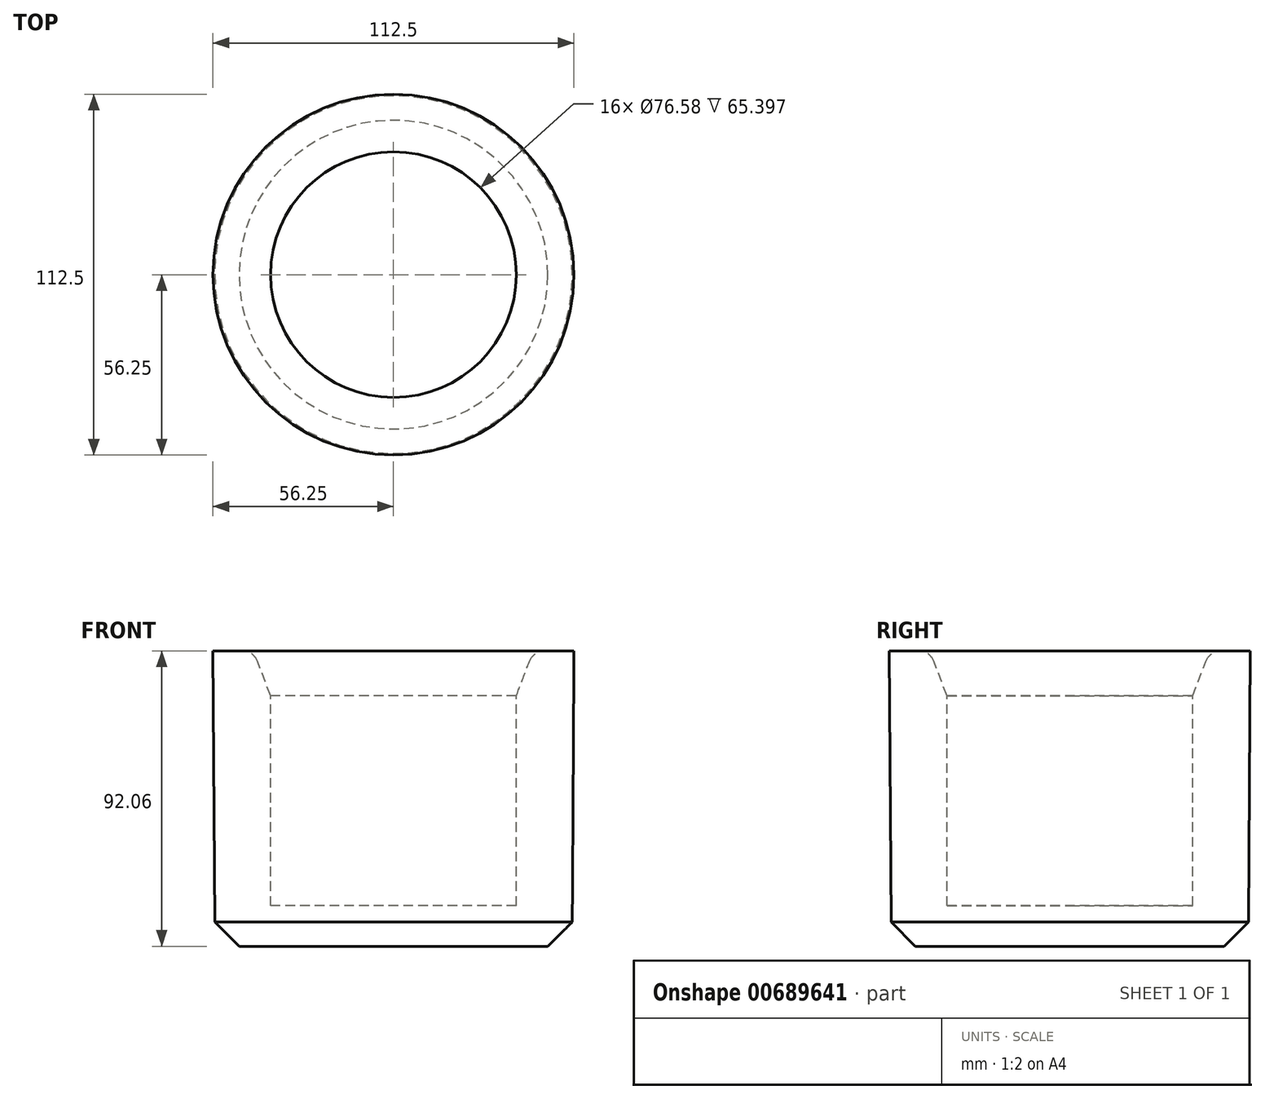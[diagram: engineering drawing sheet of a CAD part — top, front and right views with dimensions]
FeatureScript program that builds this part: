
annotation { "Feature Type Name" : "Feature", "Feature Type Description" : "" }
export const myFeature = defineFeature(function(context is Context, id is Id, definition is map)
    precondition{}
    {
        {
            var Q0;
            Q0=qCreatedBy(makeId("Front.planeOp"),FACE);
            var sketch = newSketch(context, id + "F0", { "sketchPlane" : qUnion([Q0])});
            skLineSegment(sketch, "E0", {"start": v(-56.25, 52.8) * mm, "end": v(-43.62, 52.8) * mm});
            skLineSegment(sketch, "E1", {"start": v(-43.62, 52.8) * mm, "end": v(-38.29, 38.77) * mm});
            skLineSegment(sketch, "E2", {"start": v(-38.29, 38.77) * mm, "end": v(-38.29, -26.63) * mm});
            skLineSegment(sketch, "E3", {"start": v(-38.29, -26.63) * mm, "end": v(0, -26.63) * mm});
            skLineSegment(sketch, "E4", {"start": v(0, -26.63) * mm, "end": v(0, -39.26) * mm});
            skLineSegment(sketch, "E5", {"start": v(0, -39.26) * mm, "end": v(-55.7, -39.26) * mm});
            skLineSegment(sketch, "E6", {"start": v(-55.7, -39.26) * mm, "end": v(-56.25, 52.8) * mm});
            skSolve(sketch);
        }
        {
            var Q0;
            Q0=makeQuery(id+"F0.imprint","IMPRINT",FACE,{"disambiguationData":[TD([[makeQuery(id+"F0.imprint","IMPRINT",EDGE,{"derivedFrom":sQuery(id+"F0.wireOp",EDGE,"E0")}),-1.0]])]});
            var Q1;
            Q1=sQuery(id+"F0.wireOp",EDGE,"E4");
            revolve(context, id + "F1", {"entities" : qUnion([Q0]), "axis" : qUnion([Q1]), "revolveType" : RevolveType.FULL});
        }
        {
            var Q0;
            Q0=makeQuery(id+"F1.opRevolve","SWEPT_EDGE",EDGE,{"disambiguationData":[OSD([sQuery(id+"F0.wireOp",EDGE,"E0"),sQuery(id+"F0.wireOp",EDGE,"E1")])]});
            fillet(context, id + "F2", {"entities" : qUnion([Q0]), "radius" : 5.08 * mm, "tangentPropagation" : true, "allowEdgeOverflow" : false});
        }
        {
            var Q0;
            Q0=makeQuery(id+"F1.opRevolve","SWEPT_EDGE",EDGE,{"disambiguationData":[OSD([sQuery(id+"F0.wireOp",EDGE,"E5"),sQuery(id+"F0.wireOp",EDGE,"E6")])]});
            chamfer(context, id + "F3", {"entities" : qUnion([Q0]), "width" : 7.62 * mm, "tangentPropagation" : true});
        }
    });
